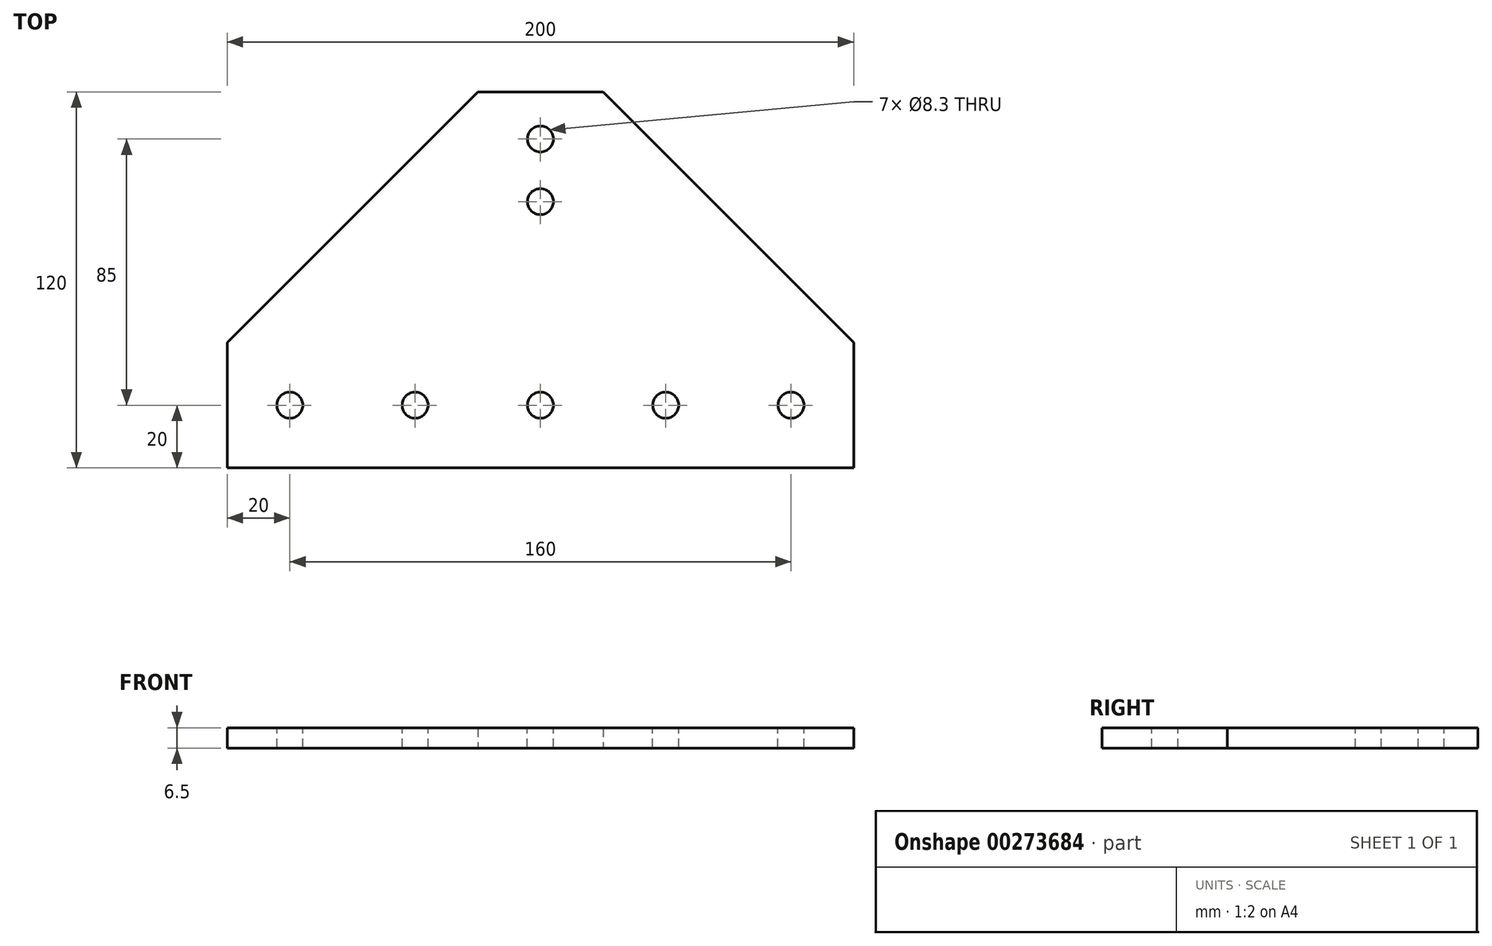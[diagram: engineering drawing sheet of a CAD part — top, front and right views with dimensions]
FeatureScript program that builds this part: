
annotation { "Feature Type Name" : "Feature", "Feature Type Description" : "" }
export const myFeature = defineFeature(function(context is Context, id is Id, definition is map)
    precondition{}
    {
        {
            var Q0;
            Q0=qCreatedBy(makeId("Top.planeOp"),FACE);
            var sketch = newSketch(context, id + "F0", { "sketchPlane" : qUnion([Q0])});
            skLineSegment(sketch, "E0", {"start": v(-100, 20) * mm, "end": v(-20, 100) * mm});
            skLineSegment(sketch, "E1", {"start": v(20, 100) * mm, "end": v(100, 20) * mm});
            skLineSegment(sketch, "E2", {"start": v(100, -20) * mm, "end": v(20, -100) * mm, "construction": true});
            skLineSegment(sketch, "E3", {"start": v(-20, -100) * mm, "end": v(-100, -20) * mm, "construction": true});
            skLineSegment(sketch, "E4", {"start": v(-20, 100) * mm, "end": v(20, 100) * mm});
            skLineSegment(sketch, "E5", {"start": v(-100, -20) * mm, "end": v(-100, 20) * mm});
            skLineSegment(sketch, "E6", {"start": v(100, 20) * mm, "end": v(100, -20) * mm});
            skLineSegment(sketch, "E7", {"start": v(-20, -100) * mm, "end": v(20, -100) * mm, "construction": true});
            skPoint(sketch, "E8.orphan", {"position": v(0, 120) * mm});
            skPoint(sketch, "E9.orphan", {"position": v(120, 0) * mm});
            skPoint(sketch, "E10.orphan", {"position": v(0, -120) * mm});
            skPoint(sketch, "E11.orphan", {"position": v(-120, 0) * mm});
            skLineSegment(sketch, "E12", {"start": v(-100, -20) * mm, "end": v(100, -20) * mm});
            skSolve(sketch);
        }
        {
            var Q0;
            Q0=qSketchRegion(id+"F0",true);
            extrude(context, id + "F1", {"entities" : qUnion([Q0]), "depth" : 6.5 * mm});
        }
        {
            var Q0;
            Q0=makeQuery(id+"F1.opExtrude","CAP_FACE",FACE,{"disambiguationData":[OSD([sQuery(id+"F0.wireOp",EDGE,"E0"),sQuery(id+"F0.wireOp",EDGE,"E1"),sQuery(id+"F0.wireOp",EDGE,"E2"),sQuery(id+"F0.wireOp",EDGE,"E3"),sQuery(id+"F0.wireOp",EDGE,"E4"),sQuery(id+"F0.wireOp",EDGE,"E5"),sQuery(id+"F0.wireOp",EDGE,"E6"),sQuery(id+"F0.wireOp",EDGE,"E7")])],"isStart":false});
            var sketch = newSketch(context, id + "F2", { "sketchPlane" : qUnion([Q0])});
            skPoint(sketch, "E13", {"position": v(0, 85) * mm});
            skPoint(sketch, "E14", {"position": v(-80, 0) * mm});
            skCircle(sketch, "E15", {"center": v(0, 42.5) * mm, "radius": 8.5 * mm, "construction": true});
            skPoint(sketch, "E16", {"position": v(0, 65) * mm});
            skLineSegment(sketch, "E17", {"start": v(-20, 20) * mm, "end": v(20, 20) * mm, "construction": true});
            skPoint(sketch, "E18", {"position": v(0, 0) * mm});
            skPoint(sketch, "E19", {"position": v(40, 0) * mm});
            skPoint(sketch, "E20", {"position": v(80, 0) * mm});
            skPoint(sketch, "E21", {"position": v(-40, 0) * mm});
            skSolve(sketch);
        }
        {
            var Q0;
            Q0=sQuery(id+"F2.wireOp",VERTEX,"E13");
            var Q1;
            Q1=sQuery(id+"F2.wireOp",VERTEX,"E16");
            var Q2;
            Q2=sQuery(id+"F2.wireOp",VERTEX,"E21");
            var Q3;
            Q3=sQuery(id+"F2.wireOp",VERTEX,"E14");
            var Q4;
            Q4=sQuery(id+"F2.wireOp",VERTEX,"E18");
            var Q5;
            Q5=sQuery(id+"F2.wireOp",VERTEX,"E19");
            var Q6;
            Q6=sQuery(id+"F2.wireOp",VERTEX,"E20");
            var Q7;
            Q7=makeQuery(id+"F1.opExtrude","SWEPT_BODY",BODY,{"disambiguationData":[OSD([sQuery(id+"F0.wireOp",EDGE,"E0"),sQuery(id+"F0.wireOp",EDGE,"E1"),sQuery(id+"F0.wireOp",EDGE,"E2"),sQuery(id+"F0.wireOp",EDGE,"E3"),sQuery(id+"F0.wireOp",EDGE,"E4"),sQuery(id+"F0.wireOp",EDGE,"E5"),sQuery(id+"F0.wireOp",EDGE,"E6"),sQuery(id+"F0.wireOp",EDGE,"E7")])]});
            hole(context, id + "F3", {"style" : HoleStyle.SIMPLE, "endStyle" : HoleEndStyle.THROUGH, "standardTappedOrClearance" : lookupTablePath({ "standard" : "ISO", "size" : "8.3", "type" : "Drilled" }), "standardBlindInLast" : lookupTablePath({ "standard" : "ISO", "size" : "8.3", "type" : "Drilled" }), "holeDiameter" : 8.3 * mm, "tappedDepth" : 12 * mm, "tapClearance" : 3, "locations" : qUnion([Q0, Q1, Q2, Q3, Q4, Q5, Q6]), "scope" : qUnion([Q7])});
        }
    });
